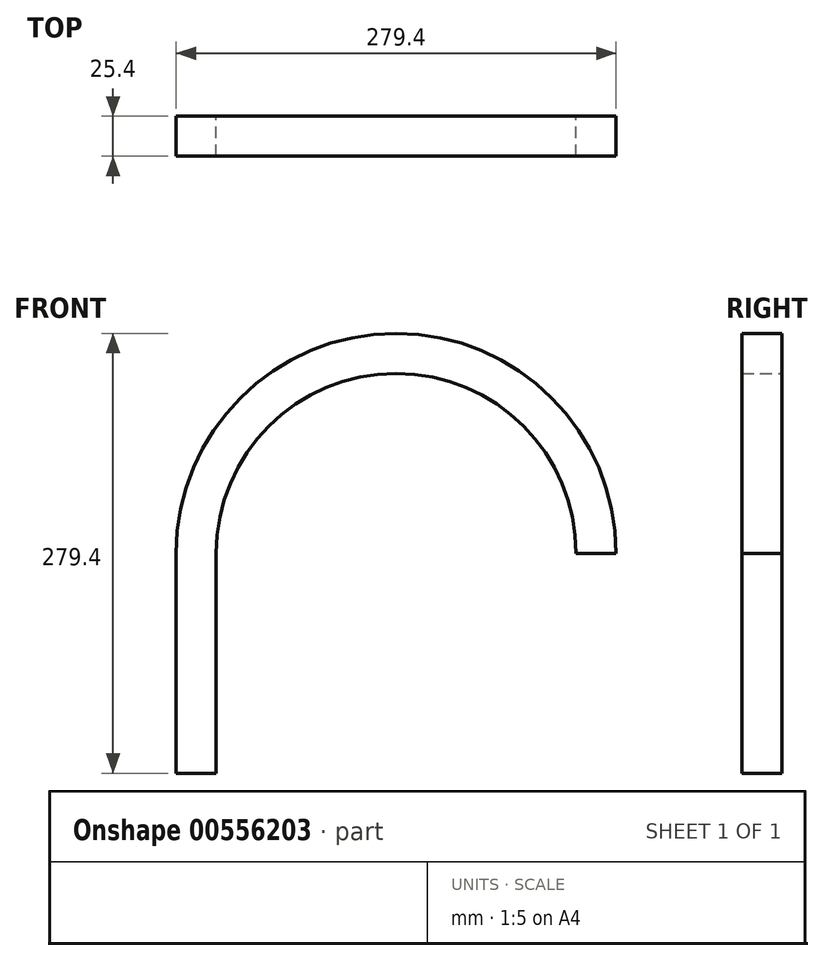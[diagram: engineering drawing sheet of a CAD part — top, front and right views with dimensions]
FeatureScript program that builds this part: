
annotation { "Feature Type Name" : "Feature", "Feature Type Description" : "" }
export const myFeature = defineFeature(function(context is Context, id is Id, definition is map)
    precondition{}
    {
        {
            var Q0;
            Q0=qCreatedBy(makeId("Front.planeOp"),FACE);
            var sketch = newSketch(context, id + "F0", { "sketchPlane" : qUnion([Q0])});
            skArc(sketch, "E0", {"start": v(139.7, 0) * mm, "mid": v(0, 139.7) * mm, "end": v(-139.7, 0) * mm});
            skArc(sketch, "E1", {"start": v(114.3, 0) * mm, "mid": v(0, 114.3) * mm, "end": v(-114.3, 0) * mm});
            skLineSegment(sketch, "E2", {"start": v(139.7, 0) * mm, "end": v(114.3, 0) * mm});
            skLineSegment(sketch, "E3", {"start": v(-139.7, 0) * mm, "end": v(-139.7, -139.7) * mm});
            skLineSegment(sketch, "E4", {"start": v(-139.7, -139.7) * mm, "end": v(-114.3, -139.7) * mm});
            skLineSegment(sketch, "E5", {"start": v(-114.3, -139.7) * mm, "end": v(-114.3, 0) * mm});
            skSolve(sketch);
        }
        {
            var Q0;
            Q0 = qSketchRegion(id + "F0", true);
            extrude(context, id + "F1", {"entities" : qUnion([Q0]), "depth" : 25.4 * mm, "offsetDistance" : 25.4 * mm});
        }
    });
